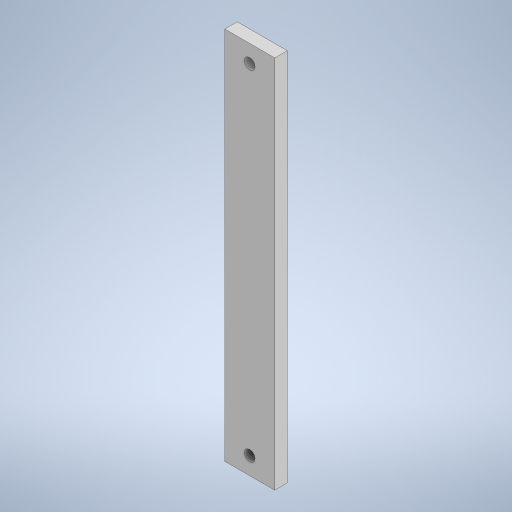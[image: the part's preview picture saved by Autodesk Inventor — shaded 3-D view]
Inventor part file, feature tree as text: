
AUTODESK INVENTOR PART (.ipt)
format: ipt  version: 2023 (Build 270158000, 158)  size: 547,840 bytes
history: native  units: mm
features: sketch x2, other x1, extrude x1, hole x1, projected_geometry x1
ambient origin geometry x8: Origin, YZ Plane, XZ Plane, XY Plane, X Axis, Y Axis, Z Axis, Center Point
bodies: Body1 (feature_tree)
feature tree (6):
  other  "Těleso1"
  extrude  "Vysunutí1"  Depth=75.0mm
  hole  "Díra1"  [1 undecoded]
  sketch  "Náčrt1"
  sketch  "Náčrt2"
  projected_geometry  "Promítnutá smyčka1"
note: 1 required parameter value undecoded (feature->parameter linkage not recoverable at this tier; creation-order binding heuristic only, values carry confidence <= 0.55)
